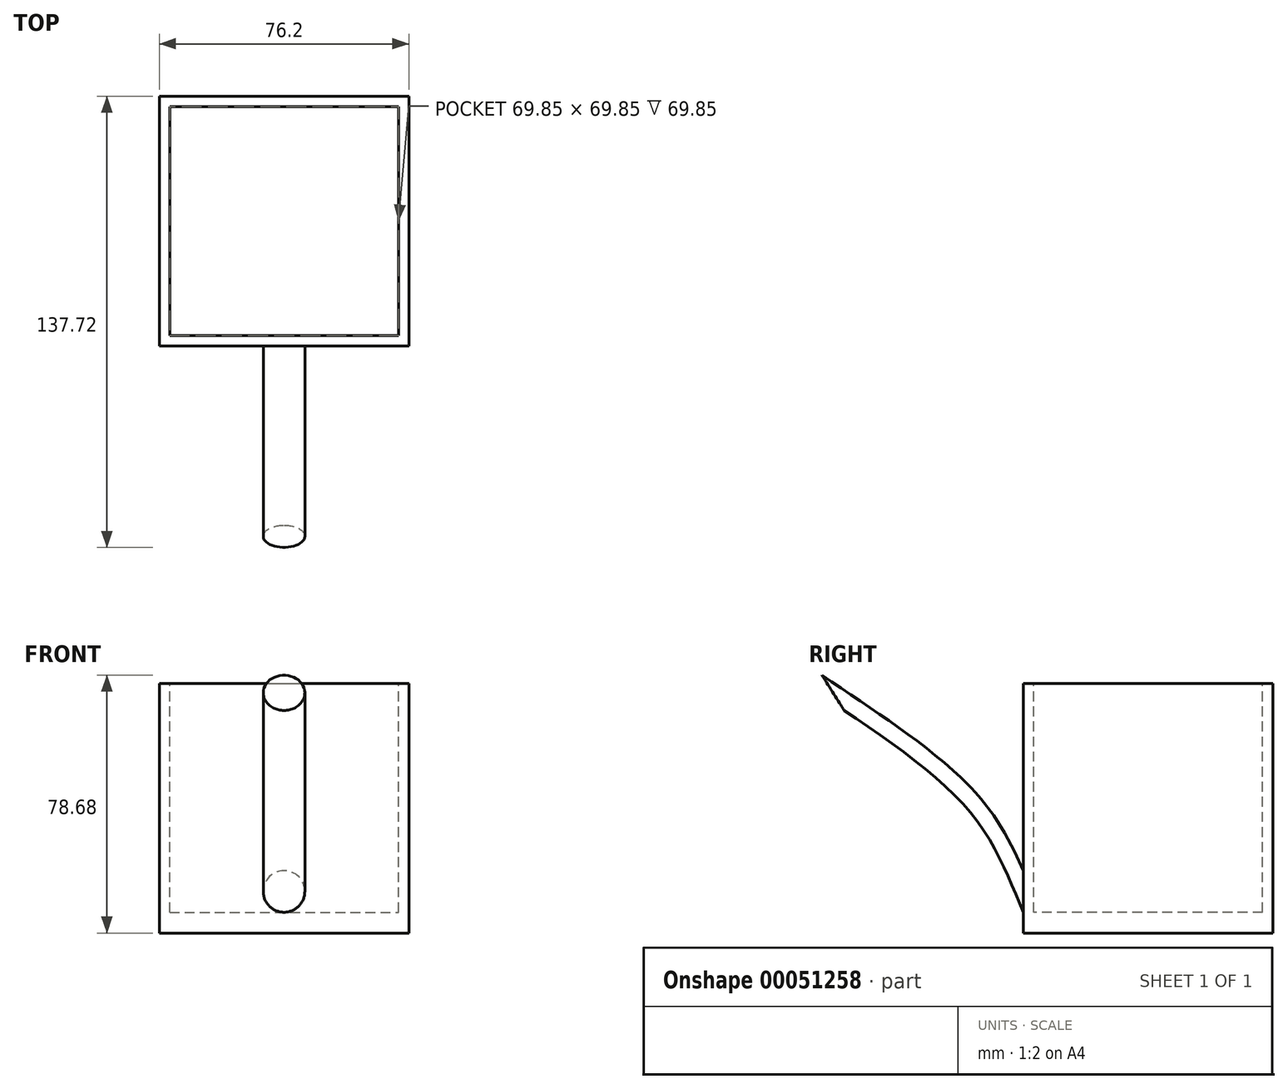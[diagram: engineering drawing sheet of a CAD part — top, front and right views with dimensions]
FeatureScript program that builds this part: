
annotation { "Feature Type Name" : "Feature", "Feature Type Description" : "" }
export const myFeature = defineFeature(function(context is Context, id is Id, definition is map)
    precondition{}
    {
        {
            var Q0;
            Q0=qCreatedBy(makeId("Top.planeOp"),FACE);
            var sketch = newSketch(context, id + "F0", { "sketchPlane" : qUnion([Q0])});
            skLineSegment(sketch, "E0.bottom", {"start": v(-37.35, 35.46) * mm, "end": v(38.85, 35.46) * mm});
            skLineSegment(sketch, "E0.top", {"start": v(-37.35, -40.74) * mm, "end": v(38.85, -40.74) * mm});
            skLineSegment(sketch, "E0.left", {"start": v(-37.35, 35.46) * mm, "end": v(-37.35, -40.74) * mm});
            skLineSegment(sketch, "E0.right", {"start": v(38.85, 35.46) * mm, "end": v(38.85, -40.74) * mm});
            skSolve(sketch);
        }
        {
            var Q0;
            Q0=makeQuery(id+"F0.imprint","IMPRINT",FACE,{"disambiguationData":[TD([[makeQuery(id+"F0.imprint","IMPRINT",EDGE,{"derivedFrom":sQuery(id+"F0.wireOp",EDGE,"E0.bottom")}),-1.0]])]});
            extrude(context, id + "F1", {"entities" : qUnion([Q0]), "depth" : 76.2 * mm});
        }
        {
            var Q0;
            Q0=makeQuery(id+"F1.opExtrude","SWEPT_FACE",FACE,{"disambiguationData":[OSD([sQuery(id+"F0.wireOp",EDGE,"E0.top")])]});
            var sketch = newSketch(context, id + "F2", { "sketchPlane" : qUnion([Q0])});
            skLineSegment(sketch, "E1", {"start": v(0.75, 76.2) * mm, "end": v(0.75, 0) * mm});
            skLineSegment(sketch, "E2", {"start": v(0.75, 0) * mm, "end": v(0.75, 76.2) * mm});
            skCircle(sketch, "E3", {"center": v(0.75, 12.7) * mm, "radius": 6.35 * mm});
            skSolve(sketch);
        }
        {
            var Q0;
            Q0=makeQuery(id+"F1.opExtrude","CAP_FACE",FACE,{"disambiguationData":[OSD([sQuery(id+"F0.wireOp",EDGE,"E0.bottom"),sQuery(id+"F0.wireOp",EDGE,"E0.top"),sQuery(id+"F0.wireOp",EDGE,"E0.left"),sQuery(id+"F0.wireOp",EDGE,"E0.right")])],"isStart":false});
            var sketch = newSketch(context, id + "F3", { "sketchPlane" : qUnion([Q0])});
            skLineSegment(sketch, "E4.bottom", {"start": v(-34.17, 32.29) * mm, "end": v(35.68, 32.29) * mm});
            skLineSegment(sketch, "E4.top", {"start": v(-34.17, -37.56) * mm, "end": v(35.68, -37.56) * mm});
            skLineSegment(sketch, "E4.left", {"start": v(-34.17, 32.29) * mm, "end": v(-34.17, -37.56) * mm});
            skLineSegment(sketch, "E4.right", {"start": v(35.68, 32.29) * mm, "end": v(35.68, -37.56) * mm});
            skSolve(sketch);
        }
        {
            var Q0;
            Q0=makeQuery(id+"F3.imprint","IMPRINT",FACE,{"disambiguationData":[TD([[makeQuery(id+"F3.imprint","IMPRINT",EDGE,{"derivedFrom":sQuery(id+"F3.wireOp",EDGE,"E4.bottom")}),-1.0]])]});
            extrude(context, id + "F4", {"entities" : qUnion([Q0]), "operationType" : NewBodyOperationType.REMOVE, "oppositeDirection" : true, "depth" : 69.85 * mm});
        }
        {
            var Q0;
            Q0=makeQuery(id+"F1.opExtrude","SWEPT_FACE",FACE,{"disambiguationData":[OSD([sQuery(id+"F0.wireOp",EDGE,"E0.right")])]});
            cPlane(context, id + "F5", {"entities" : qUnion([Q0]), "cplaneType" : CPlaneType.OFFSET, "offset" : 38.1 * mm, "oppositeDirection" : true, "width" : 152.4 * mm, "height" : 152.4 * mm});
        }
        {
            var Q0;
            Q0=qCreatedBy(id+"F5.planeOp",FACE);
            var sketch = newSketch(context, id + "F6", { "sketchPlane" : qUnion([Q0])});
            skPoint(sketch, "E5", {"position": v(-40.74, 12.7) * mm});
            skFitSpline(sketch, "E6", {"points": [v(-40.74, 12.7) * mm, v(-56.56, 40) * mm, v(-98.87, 73.3) * mm], "startDerivative": vector(-28.2, 63.87) * mm, "endDerivative": vector(-85.53, 57.62) * mm});
            skSolve(sketch);
        }
        {
            var Q0;
            Q0 = qSketchRegion(id + "F2", true);
            var Q1;
            Q1 = qConstructionFilter(qBodyType(qCreatedBy(id + "F6" ,EDGE), BodyType.WIRE), ConstructionObject.NO);
            sweep(context, id + "F7", {"operationType" : NewBodyOperationType.ADD, "profiles" : qUnion([Q0]), "path" : qUnion([Q1])});
        }
    });
